# Revit family: 303_R435TGX_
name_source: partatom
category: Pipe Accessories
revit_build: Autodesk Revit 2018 (Build: 20170223_1515(x64)
units: mm (PartAtom-declared; Revit-internal decimal feet)

## family parameters
Always vertical = Yes
Cut with Voids When Loaded = No
Part Type = Valve - Breaks Into
Round Connector Dimension = Use Diameter
Shared = No
Work Plane-Based = No

## types (3) — shared parameters
CAT0 = Yes
CenSd_K1_6 = 11 mm
CenSd_W3_6 = 13 mm
D = 15 mm
Description = Micrometric angle valve with thermostatic option, with presetting
J1 = 7 mm  [stored 0.0229659 ft]
K1 = 13 mm
K2 = 10 mm  [stored 0.0328084 ft]
L2D_Min = 3048 mm  [stored 10 ft]
M1 = 21 mm  [stored 0.0688976 ft]
Manufacturer = Giacomini
QmdConnectorList = 301;D;302;D1
URL = http://www.giacomini.com
W1 = 5 mm  [stored 0.0164042 ft]
W2 = 12 mm  [stored 0.0393701 ft]
W2D = 15 mm  [stored 0.0492126 ft]
W3 = 15 mm  [stored 0.0492126 ft]
W4 = 8 mm  [stored 0.0262467 ft]
Z1 = 10 mm  [stored 0.0328084 ft]
magiPartTypeId = 303
magiProductFamilyId = R435TGX*
zero-valued in all types: MC_Default_elevation

## per-type parameters (varying)
| type | D1 | G1 | J | J2 | J3 | L | L1 | L2 | L2D | L5 | L6 | LT1 | LT1__ve | LT2 | LT2__ve | R | SW | SW1 |
| R435X033 | 15 mm | 13 mm | 36 mm  [stored 0.11811 ft] | 5 mm  [stored 0.0164042 ft] | 23 mm  [stored 0.0754593 ft] | 53 mm  [stored 0.173885 ft] | 13 mm | 27 mm | 53 mm  [stored 0.173885 ft] | 18 mm | 9 mm  [stored 0.0295276 ft] | 23 mm  [stored 0.0754593 ft] | -23 mm  [stored -0.0754593 ft] | 35 mm | -35 mm | 11 mm | No | Yes |
| R435X043 | 18 mm | 16 mm | 37 mm | 6 mm  [stored 0.019685 ft] | 24 mm | 45 mm | 11 mm | 23 mm  [stored 0.0754593 ft] | 45 mm | 15 mm  [stored 0.0492126 ft] | 7 mm  [stored 0.0229659 ft] | 22 mm | -22 mm | 33 mm | -33 mm | 13 mm | Yes | No |
| R435X042 | 16 mm | 16 mm | 36 mm  [stored 0.11811 ft] | 5 mm  [stored 0.0164042 ft] | 23 mm  [stored 0.0754593 ft] | 45 mm | 11 mm | 23 mm  [stored 0.0754593 ft] | 45 mm | 15 mm  [stored 0.0492126 ft] | 7 mm  [stored 0.0229659 ft] | 22 mm | -22 mm | 33 mm | -33 mm | 13 mm | Yes | No |

note: column(s) folded — value = type name in every type: magiProductCode, magiProductId

note: [stored X ft] marks values corroborated as IEEE doubles in the binary element streams (Revit-internal decimal feet)

## geometry (parser evidence)
native form markers: Sweep x1
no freeform markers — native parametric forms only
